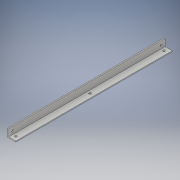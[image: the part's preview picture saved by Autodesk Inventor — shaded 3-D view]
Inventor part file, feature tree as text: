
AUTODESK INVENTOR PART (.ipt)
format: ipt  version: 2017 (Build 210142000, 142)  size: 128,512 bytes
history: native  units: in
note: dims shown in document units (in); Inventor stores cm internally (conversion verified against a paired STEP export)
features: hole x3, sketch x3, extrude x1
ambient origin geometry x8: Origin, YZ Plane, XZ Plane, XY Plane, X Axis, Y Axis, Z Axis, Center Point
bodies: Solid1 (feature_tree)
feature tree (7):
  extrude  "Extrusion1"  Depth=1.0in
  hole  "rail"  [1 undecoded]
  hole  "mount"  [1 undecoded]
  hole  "Hole5"  [1 undecoded]
  sketch  "Sketch2"  dims[d0=1.0in d1=1.0in]
  sketch  "Sketch7"  dims[d2=0.125in d3=19.375in d4=0.0in]
  sketch  "Sketch8"  dims[d5=0.5in d6=0.5in d7=0.7874in d9=18.375in d10=0.3937in d12=1.0in d14=0.266in d15=0.75in d16=0.385in d17=0.25in d18=0.5635in d19=1.0in d20=0.8108in d31=0.5in d43=0.5in d44=0.5in d45=0.7874in d47=18.375in d48=0.3937in d50=1.0in d52=0.266in d53=0.75in d54=0.507in d55=0.25in d56=0.5635in d57=1.0in d58=0.8108in d59=0.266in d60=0.75in d61=0.507in d62=0.25in d63=0.5635in d64=1.0in d65=0.8108in]
note: 3 required parameter values undecoded (feature->parameter linkage not recoverable at this tier; creation-order binding heuristic only, values carry confidence <= 0.55)
